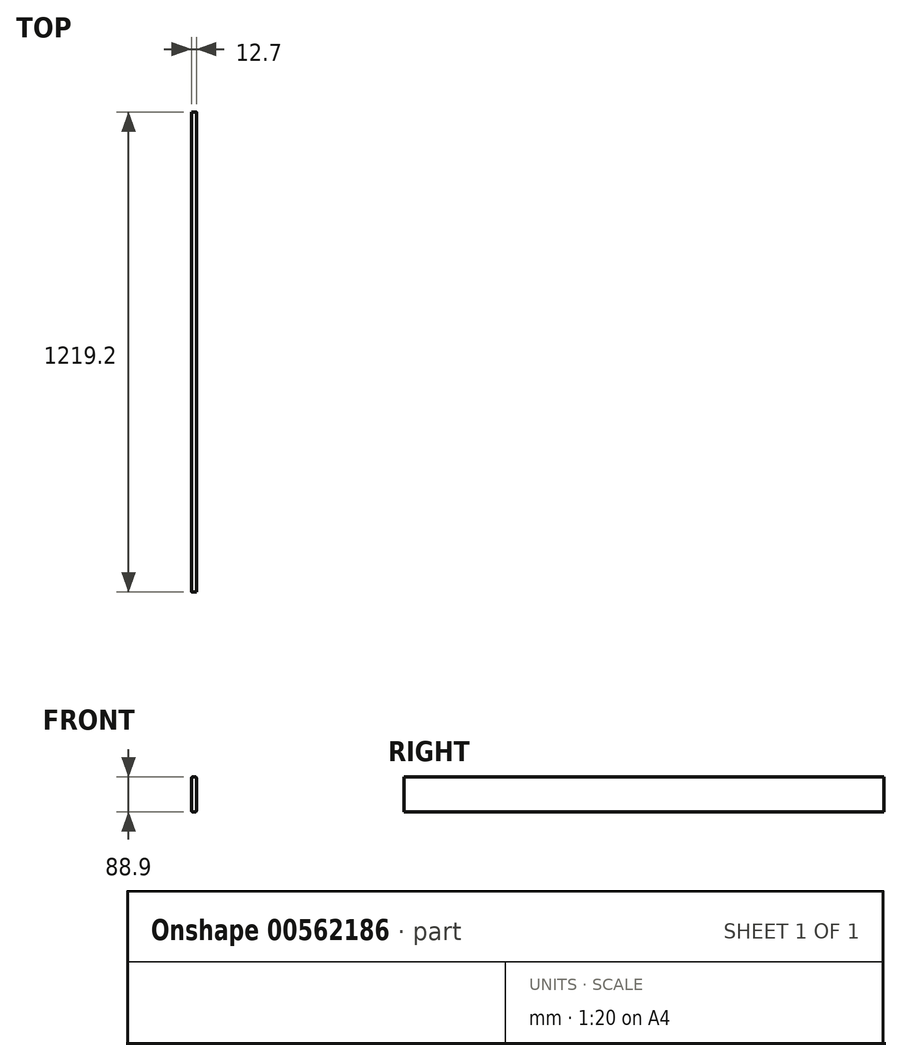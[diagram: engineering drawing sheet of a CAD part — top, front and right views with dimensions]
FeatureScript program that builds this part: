
annotation { "Feature Type Name" : "Feature", "Feature Type Description" : "" }
export const myFeature = defineFeature(function(context is Context, id is Id, definition is map)
    precondition{}
    {
        {
            var Q0;
            Q0=qCreatedBy(makeId("Front.planeOp"),FACE);
            var sketch = newSketch(context, id + "F0", { "sketchPlane" : qUnion([Q0])});
            skLineSegment(sketch, "E0.bottom", {"start": v(-3.17, 44.45) * mm, "end": v(3.17, 44.45) * mm});
            skLineSegment(sketch, "E0.top", {"start": v(-3.17, -44.45) * mm, "end": v(3.17, -44.45) * mm});
            skLineSegment(sketch, "E0.left", {"start": v(-6.35, 41.28) * mm, "end": v(-6.35, -41.28) * mm});
            skLineSegment(sketch, "E0.right", {"start": v(6.35, 41.28) * mm, "end": v(6.35, -41.28) * mm});
            skPoint(sketch, "E1.visualSharp", {"position": v(-6.35, 44.45) * mm});
            skArc(sketch, "E1.filletArc", {"start": v(-3.17, 44.45) * mm, "mid": v(-5.42, 43.52) * mm, "end": v(-6.35, 41.28) * mm});
            skPoint(sketch, "E2.visualSharp", {"position": v(6.35, 44.45) * mm});
            skArc(sketch, "E2.filletArc", {"start": v(6.35, 41.28) * mm, "mid": v(5.42, 43.52) * mm, "end": v(3.17, 44.45) * mm});
            skPoint(sketch, "E3.visualSharp", {"position": v(-6.35, -44.45) * mm});
            skArc(sketch, "E3.filletArc", {"start": v(-6.35, -41.28) * mm, "mid": v(-5.42, -43.52) * mm, "end": v(-3.17, -44.45) * mm});
            skPoint(sketch, "E4.visualSharp", {"position": v(6.35, -44.45) * mm});
            skArc(sketch, "E4.filletArc", {"start": v(3.17, -44.45) * mm, "mid": v(5.42, -43.52) * mm, "end": v(6.35, -41.28) * mm});
            skLineSegment(sketch, "E5", {"start": v(0, 0) * mm, "end": v(0, -44.45) * mm, "construction": true});
            skLineSegment(sketch, "E6", {"start": v(0, 0) * mm, "end": v(-6.35, 0) * mm, "construction": true});
            skSolve(sketch);
        }
        {
            var Q0;
            Q0=makeQuery(id+"F0.imprint","IMPRINT",FACE,{"disambiguationData":[TD([[makeQuery(id+"F0.imprint","IMPRINT",EDGE,{"derivedFrom":sQuery(id+"F0.wireOp",EDGE,"E0.bottom")}),-1.0]])]});
            extrude(context, id + "F1", {"entities" : qUnion([Q0]), "depth" : 1219.2 * mm, "offsetDistance" : 25.4 * mm});
        }
    });
